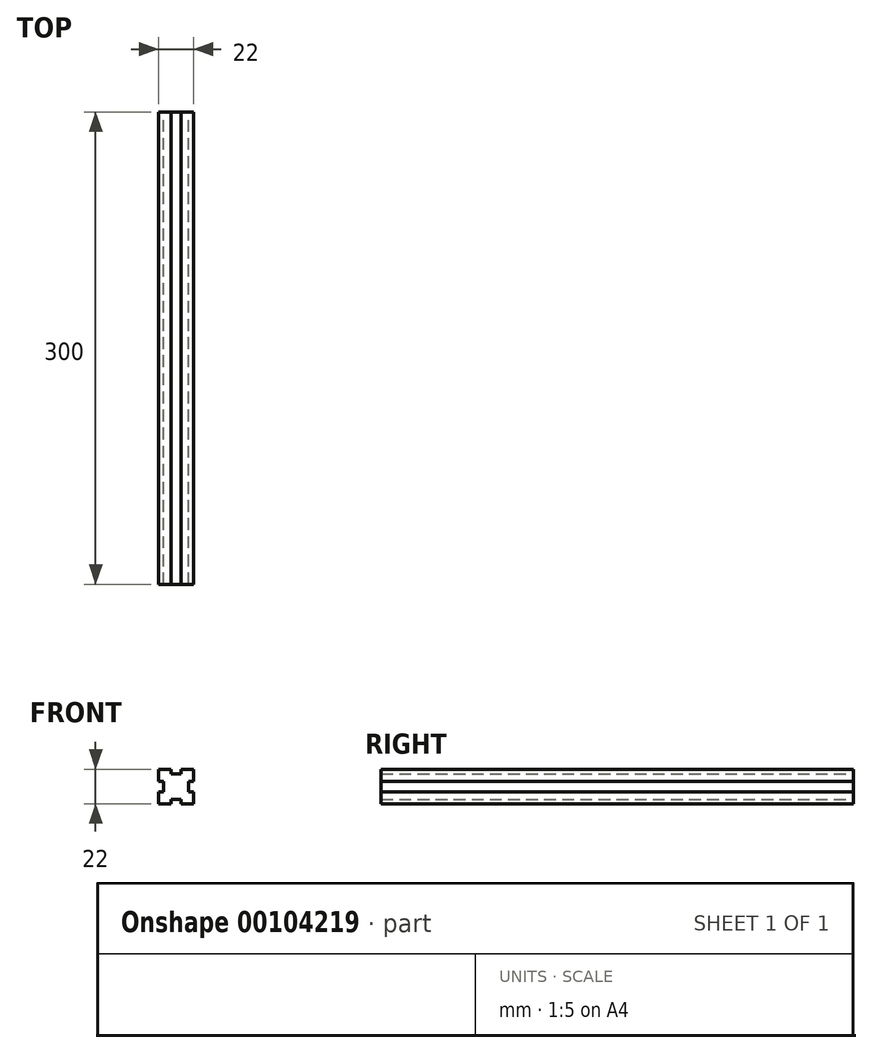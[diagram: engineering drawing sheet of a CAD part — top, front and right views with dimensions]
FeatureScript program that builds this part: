
annotation { "Feature Type Name" : "Feature", "Feature Type Description" : "" }
export const myFeature = defineFeature(function(context is Context, id is Id, definition is map)
    precondition{}
    {
        {
            var Q0;
            Q0=qCreatedBy(makeId("Front.planeOp"),FACE);
            var sketch = newSketch(context, id + "F0", { "sketchPlane" : qUnion([Q0])});
            skLineSegment(sketch, "E0", {"start": v(0, 0) * mm, "end": v(7.75, 0) * mm});
            skLineSegment(sketch, "E1", {"start": v(7.75, 0) * mm, "end": v(7.75, -3) * mm});
            skLineSegment(sketch, "E2", {"start": v(7.75, -3) * mm, "end": v(14.25, -3) * mm});
            skLineSegment(sketch, "E3", {"start": v(14.25, -3) * mm, "end": v(14.25, 0) * mm});
            skLineSegment(sketch, "E4", {"start": v(14.25, 0) * mm, "end": v(22, 0) * mm});
            skLineSegment(sketch, "E5", {"start": v(22, 0) * mm, "end": v(22, -7.75) * mm});
            skLineSegment(sketch, "E6", {"start": v(22, -7.75) * mm, "end": v(19, -7.75) * mm});
            skLineSegment(sketch, "E7", {"start": v(19, -7.75) * mm, "end": v(19, -14.25) * mm});
            skLineSegment(sketch, "E8", {"start": v(19, -14.25) * mm, "end": v(22, -14.25) * mm});
            skLineSegment(sketch, "E9", {"start": v(22, -14.25) * mm, "end": v(22, -22) * mm});
            skLineSegment(sketch, "E10", {"start": v(22, -22) * mm, "end": v(14.25, -22) * mm});
            skLineSegment(sketch, "E11", {"start": v(14.25, -22) * mm, "end": v(14.25, -19) * mm});
            skLineSegment(sketch, "E12", {"start": v(14.25, -19) * mm, "end": v(7.75, -19) * mm});
            skLineSegment(sketch, "E13", {"start": v(7.75, -19) * mm, "end": v(7.75, -22) * mm});
            skLineSegment(sketch, "E14", {"start": v(7.75, -22) * mm, "end": v(0, -22) * mm});
            skLineSegment(sketch, "E15", {"start": v(0, -22) * mm, "end": v(0, -14.25) * mm});
            skLineSegment(sketch, "E16", {"start": v(0, -14.25) * mm, "end": v(3, -14.25) * mm});
            skLineSegment(sketch, "E17", {"start": v(3, -14.25) * mm, "end": v(3, -7.75) * mm});
            skLineSegment(sketch, "E18", {"start": v(3, -7.75) * mm, "end": v(0, -7.75) * mm});
            skLineSegment(sketch, "E19", {"start": v(0, -7.75) * mm, "end": v(0, 0) * mm});
            skSolve(sketch);
        }
        {
            var Q0;
            Q0=makeQuery(id+"F0.imprint","IMPRINT",FACE,{"disambiguationData":[TD([[makeQuery(id+"F0.imprint","IMPRINT",EDGE,{"derivedFrom":sQuery(id+"F0.wireOp",EDGE,"E0")}),-1.0]])]});
            extrude(context, id + "F1", {"entities" : qUnion([Q0]), "depth" : 300 * mm});
        }
    });
